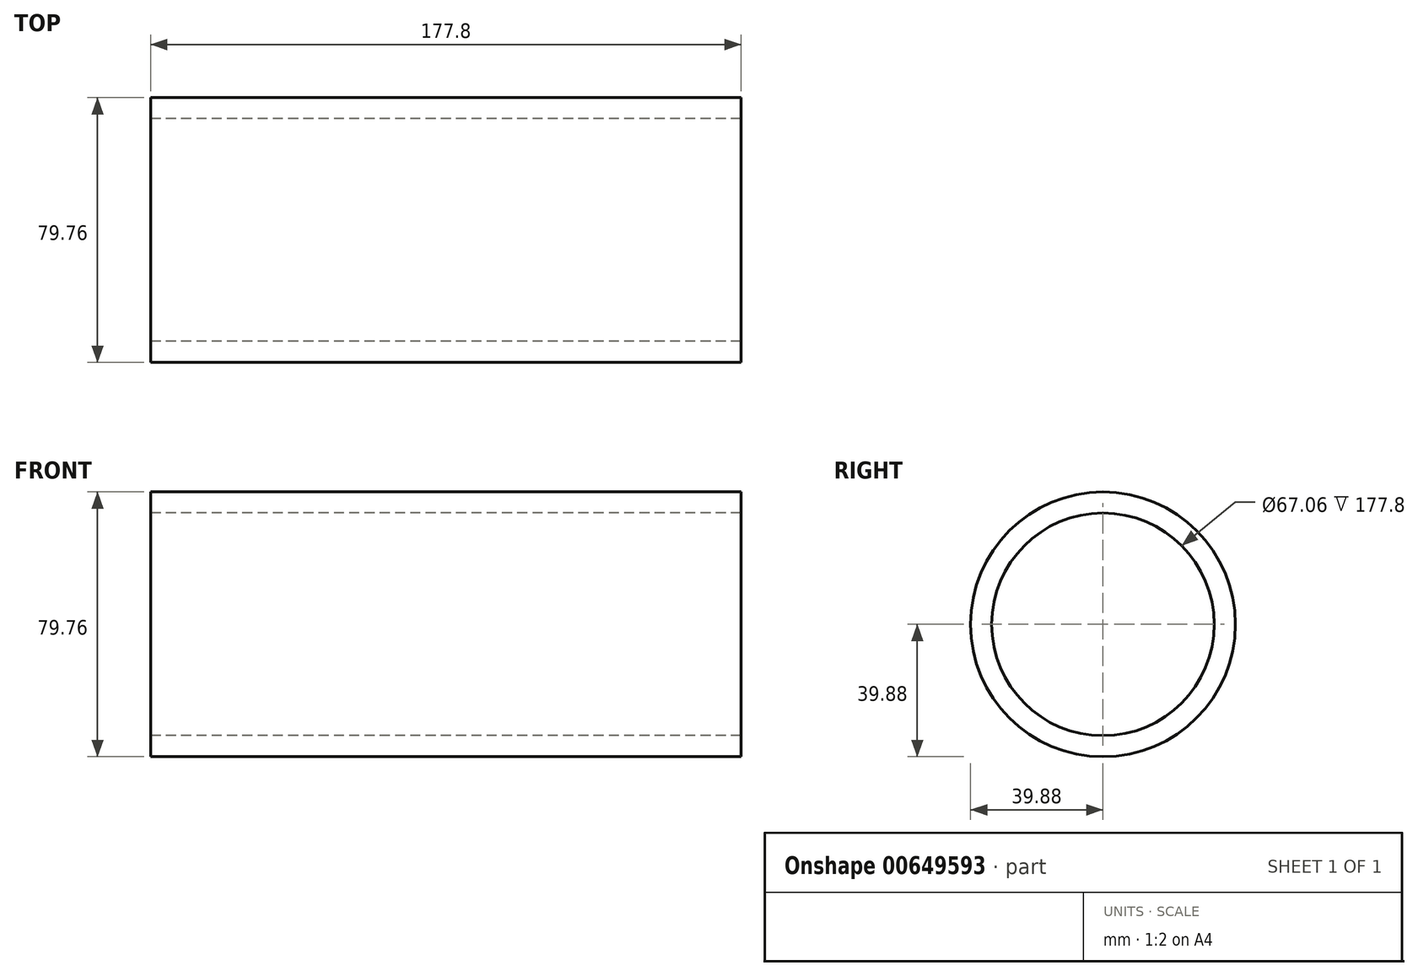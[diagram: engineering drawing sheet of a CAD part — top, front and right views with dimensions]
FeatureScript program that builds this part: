
annotation { "Feature Type Name" : "Feature", "Feature Type Description" : "" }
export const myFeature = defineFeature(function(context is Context, id is Id, definition is map)
    precondition{}
    {
        {
            var Q0;
            Q0=qCreatedBy(makeId("Right.planeOp"),FACE);
            var sketch = newSketch(context, id + "F0", { "sketchPlane" : qUnion([Q0])});
            skCircle(sketch, "E0", {"center": v(0, 0) * mm, "radius": 39.88 * mm});
            skCircle(sketch, "E1", {"center": v(0, 0) * mm, "radius": 33.53 * mm});
            skSolve(sketch);
        }
        {
            var Q0;
            Q0 = qSketchRegion(id + "F0", true);
            var Q1;
            Q1=makeQuery(id+"F0.imprint","IMPRINT",FACE,{"disambiguationData":[TD([[makeQuery(id+"F0.imprint","IMPRINT",EDGE,{"derivedFrom":sQuery(id+"F0.wireOp",EDGE,"E0")}),1.0]])]});
            extrude(context, id + "F1", {"entities" : qUnion([Q0, Q1]), "depth" : 177.8 * mm, "offsetDistance" : 25.4 * mm});
        }
    });
